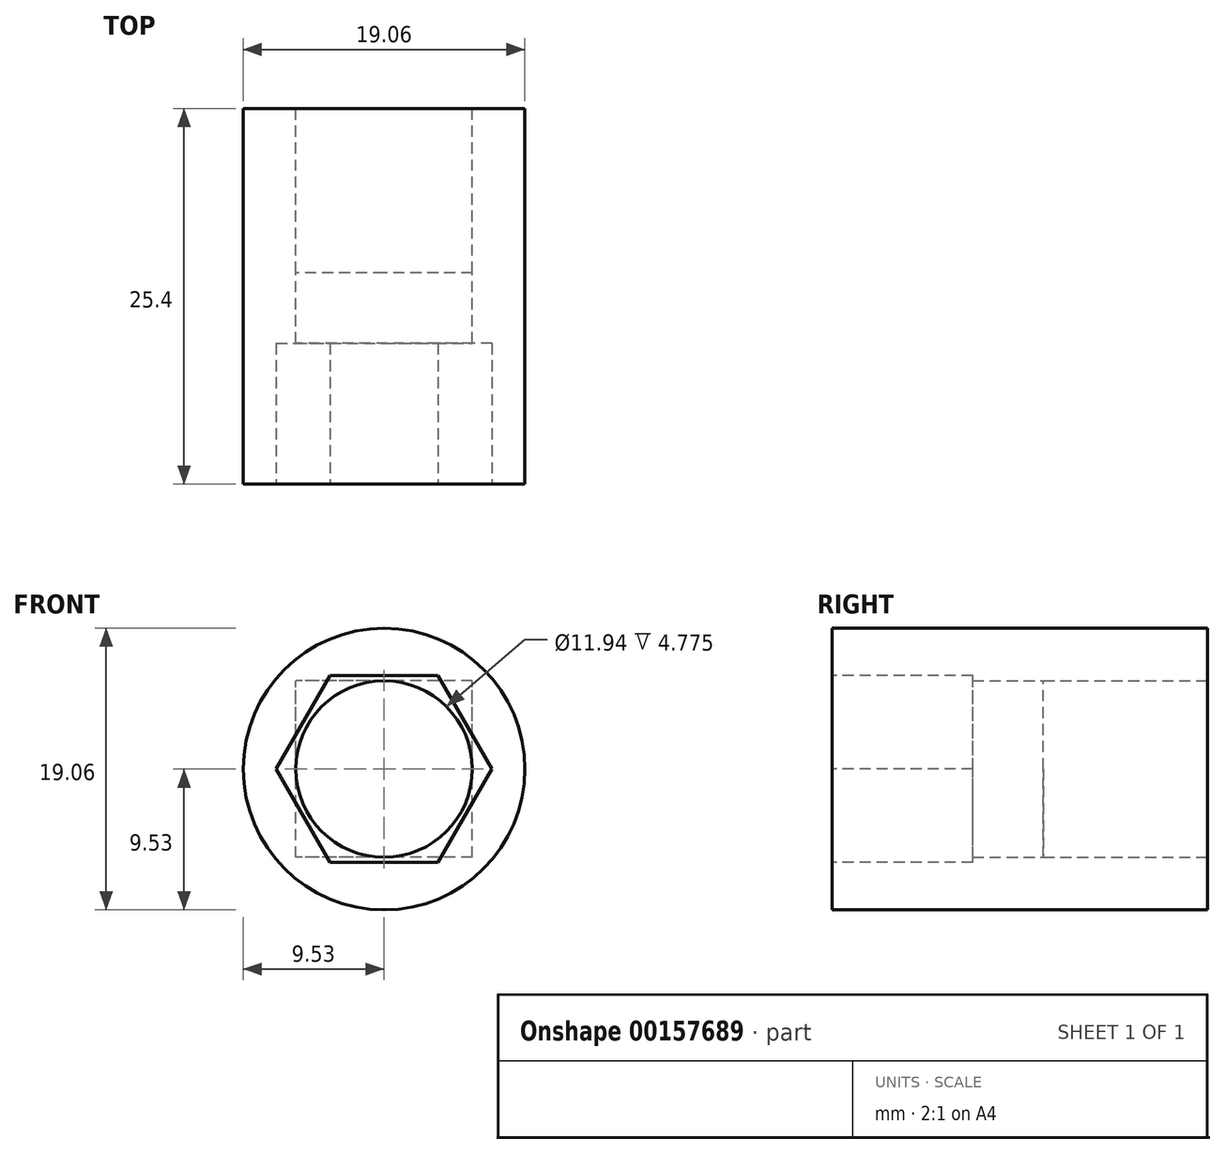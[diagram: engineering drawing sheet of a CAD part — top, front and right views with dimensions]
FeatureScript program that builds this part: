
annotation { "Feature Type Name" : "Feature", "Feature Type Description" : "" }
export const myFeature = defineFeature(function(context is Context, id is Id, definition is map)
    precondition{}
    {
        {
            var Q0;
            Q0=qCreatedBy(makeId("Front.planeOp"),FACE);
            var sketch = newSketch(context, id + "F0", { "sketchPlane" : qUnion([Q0])});
            skCircle(sketch, "E0", {"center": v(0, 0) * mm, "radius": 9.53 * mm});
            skSolve(sketch);
        }
        {
            var Q0;
            Q0 = qSketchRegion(id + "F0", true);
            extrude(context, id + "F1", {"entities" : qUnion([Q0]), "depth" : 25.4 * mm});
        }
        {
            var Q0;
            Q0=qCreatedBy(makeId("Front.planeOp"),FACE);
            var sketch = newSketch(context, id + "F2", { "sketchPlane" : qUnion([Q0])});
            skLineSegment(sketch, "E1.bottom", {"start": v(5.97, -5.97) * mm, "end": v(-5.97, -5.97) * mm});
            skLineSegment(sketch, "E1.top", {"start": v(5.97, 5.97) * mm, "end": v(-5.97, 5.97) * mm});
            skLineSegment(sketch, "E1.left", {"start": v(5.97, -5.97) * mm, "end": v(5.97, 5.97) * mm});
            skLineSegment(sketch, "E1.right", {"start": v(-5.97, -5.97) * mm, "end": v(-5.97, 5.97) * mm});
            skPoint(sketch, "E1.middle", {"position": v(0, 0) * mm});
            skSolve(sketch);
        }
        {
            var Q0;
            Q0=qCreatedBy(makeId("Front.planeOp"),FACE);
            var sketch = newSketch(context, id + "F3", { "sketchPlane" : qUnion([Q0])});
            skCircle(sketch, "E2", {"center": v(0, 0) * mm, "radius": 5.97 * mm});
            skSolve(sketch);
        }
        {
            var Q0;
            Q0 = qSketchRegion(id + "F3", true);
            extrude(context, id + "F4", {"entities" : qUnion([Q0]), "operationType" : NewBodyOperationType.REMOVE, "endBound" : BoundingType.THROUGH_ALL, "depth" : 25.4 * mm});
        }
        {
            var Q0;
            Q0 = qSketchRegion(id + "F2", true);
            extrude(context, id + "F5", {"entities" : qUnion([Q0]), "operationType" : NewBodyOperationType.REMOVE, "depth" : 11.1 * mm});
        }
        {
            var Q0;
            Q0=makeQuery(id+"F1.opExtrude","CAP_FACE",FACE,{"disambiguationData":[OSD([sQuery(id+"F0.wireOp",EDGE,"E0")])],"isStart":false});
            var sketch = newSketch(context, id + "F6", { "sketchPlane" : qUnion([Q0])});
            skCircle(sketch, "E3.cCircle", {"center": v(0, 0) * mm, "radius": 6.32 * mm, "construction": true});
            skLineSegment(sketch, "E3.0", {"start": v(-3.65, 6.32) * mm, "end": v(3.65, 6.32) * mm});
            skLineSegment(sketch, "E3.1", {"start": v(3.65, 6.32) * mm, "end": v(7.3, 0) * mm});
            skLineSegment(sketch, "E3.2", {"start": v(7.3, 0) * mm, "end": v(3.65, -6.32) * mm});
            skLineSegment(sketch, "E3.3", {"start": v(3.65, -6.32) * mm, "end": v(-3.65, -6.32) * mm});
            skLineSegment(sketch, "E3.4", {"start": v(-3.65, -6.32) * mm, "end": v(-7.3, 0) * mm});
            skLineSegment(sketch, "E3.5", {"start": v(-7.3, 0) * mm, "end": v(-3.65, 6.32) * mm});
            skPoint(sketch, "E3.0.midPoint", {"position": v(0, 6.32) * mm});
            skSolve(sketch);
        }
        {
            var Q0;
            Q0 = qSketchRegion(id + "F6", true);
            extrude(context, id + "F7", {"entities" : qUnion([Q0]), "operationType" : NewBodyOperationType.REMOVE, "oppositeDirection" : true, "depth" : 9.52 * mm});
        }
    });
